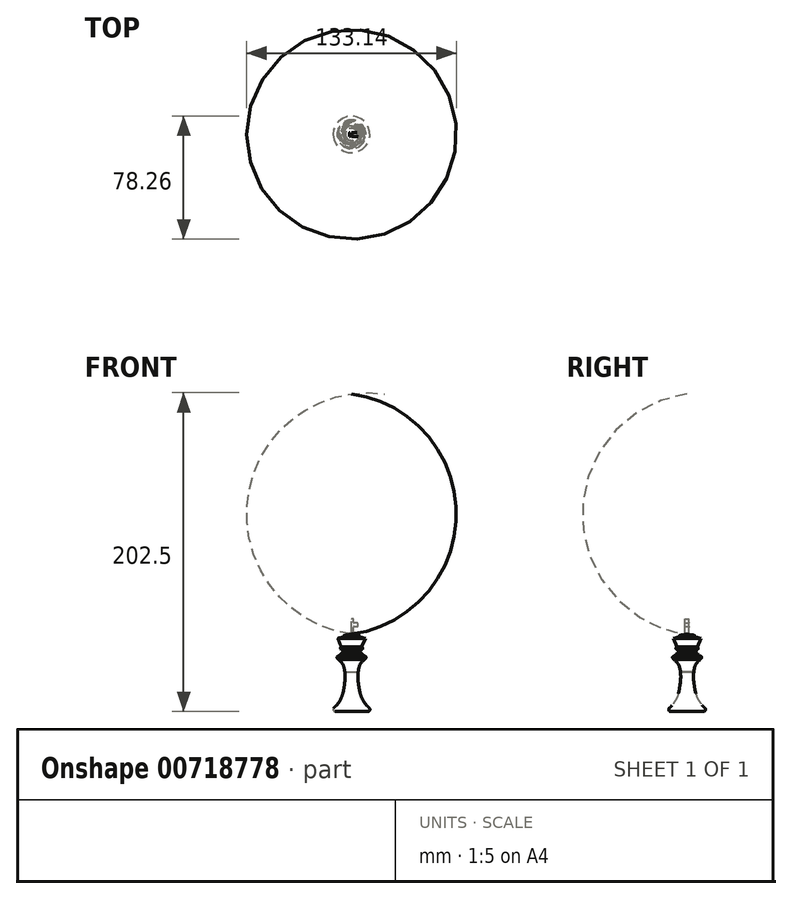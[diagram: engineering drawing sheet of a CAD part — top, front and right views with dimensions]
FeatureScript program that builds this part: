
annotation { "Feature Type Name" : "Feature", "Feature Type Description" : "" }
export const myFeature = defineFeature(function(context is Context, id is Id, definition is map)
    precondition{}
    {
        {
            var Q0;
            Q0=qCreatedBy(makeId("Front.planeOp"),FACE);
            var sketch = newSketch(context, id + "F0", { "sketchPlane" : qUnion([Q0])});
            skLineSegment(sketch, "E0", {"start": v(-6.27, -38.45) * mm, "end": v(13.97, -38.45) * mm});
            skLineSegment(sketch, "E1", {"start": v(9.14, -4.26) * mm, "end": v(9.14, -3.81) * mm});
            skLineSegment(sketch, "E2", {"start": v(7.58, -3.05) * mm, "end": v(5.64, -3.05) * mm});
            skLineSegment(sketch, "E3", {"start": v(5.15, -0.78) * mm, "end": v(5.9, 1.02) * mm});
            skLineSegment(sketch, "E4.MirrorCS", {"start": v(-10.7, 7.6) * mm, "end": v(-5.3, 8.78) * mm});
            skLineSegment(sketch, "E5.MirrorCS", {"start": v(-5.15, -0.78) * mm, "end": v(-8, 8.18) * mm});
            skLineSegment(sketch, "E6.MirrorCS", {"start": v(-7.58, -3.05) * mm, "end": v(-5.64, -3.05) * mm});
            skLineSegment(sketch, "E7.MirrorCS", {"start": v(-9.14, -4.26) * mm, "end": v(-9.14, -3.81) * mm});
            skLineSegment(sketch, "E8.MirrorCS", {"start": v(6.27, -38.45) * mm, "end": v(-13.97, -38.45) * mm});
            skFitSpline(sketch, "E9", {"points": [v(13.97, -38.45) * mm, v(4.51, -21.56) * mm, v(13.97, -2.87) * mm], "startDerivative": vector(-46, 33.89) * mm, "endDerivative": vector(65.38, 22.38) * mm});
            skFitSpline(sketch, "E10.MirrorCS", {"points": [v(-13.97, -38.45) * mm, v(-4.51, -21.56) * mm, v(-13.97, -2.87) * mm], "startDerivative": vector(46, 33.89) * mm, "endDerivative": vector(-65.38, 22.38) * mm});
            skPoint(sketch, "E11.orphan", {"position": v(-9.68, -5.46) * mm});
            skFitSpline(sketch, "E12", {"points": [v(-8.26, -5.46) * mm, v(-4.22, -13.38) * mm], "startDerivative": vector(8.52, -8.35) * mm, "endDerivative": vector(2.36, -15.7) * mm});
            skPoint(sketch, "E13.MirrorP", {"position": v(9.68, -5.46) * mm});
            skFitSpline(sketch, "E14.MirrorCS", {"points": [v(13.97, -38.45) * mm, v(4.51, -21.56) * mm, v(13.97, -2.87) * mm], "startDerivative": vector(-46, 33.89) * mm, "endDerivative": vector(65.38, 22.38) * mm});
            skPoint(sketch, "E15.MirrorCS.1.internal.orphan", {"position": v(4.22, -13.38) * mm});
            skPoint(sketch, "E15.MirrorCS.start.orphan", {"position": v(8.26, -5.46) * mm});
            skFitSpline(sketch, "E16.MirrorCS", {"points": [v(8.26, -5.46) * mm, v(4.22, -13.38) * mm], "startDerivative": vector(-8.52, -8.35) * mm, "endDerivative": vector(-2.36, -15.7) * mm});
            skPoint(sketch, "E17.1.internal.snap0", {"position": v(6.88, 3.45) * mm});
            skFitSpline(sketch, "E17", {"points": [v(5.15, -0.78) * mm, v(6.88, -1.91) * mm, v(5.64, -3.05) * mm], "startDerivative": vector(0.14, -3.1) * mm, "endDerivative": vector(-12.3, 0) * mm});
            skPoint(sketch, "E18.orphan", {"position": v(4.22, -3.05) * mm});
            skFitSpline(sketch, "E19.MirrorCS", {"points": [v(-5.15, -0.78) * mm, v(-6.88, -1.91) * mm, v(-5.64, -3.05) * mm], "startDerivative": vector(-0.14, -3.1) * mm, "endDerivative": vector(12.3, 0) * mm});
            skPoint(sketch, "E20.orphan", {"position": v(-4.42, -3.08) * mm});
            skPoint(sketch, "E21.orphan", {"position": v(-4.22, -3.05) * mm});
            skFitSpline(sketch, "E22", {"points": [v(7.58, -3.05) * mm, v(9.14, -4.26) * mm, v(8.26, -5.46) * mm], "startDerivative": vector(8.74, -1.07) * mm, "endDerivative": vector(-3.54, -2.6) * mm});
            skPoint(sketch, "E23.MirrorCS.start.orphan", {"position": v(9.14, -5.46) * mm});
            skPoint(sketch, "E24.orphan", {"position": v(9.14, -3.05) * mm});
            skFitSpline(sketch, "E25.MirrorCS", {"points": [v(-7.58, -3.05) * mm, v(-9.14, -4.26) * mm, v(-8.26, -5.46) * mm], "startDerivative": vector(-8.74, -1.07) * mm, "endDerivative": vector(3.54, -2.6) * mm});
            skPoint(sketch, "E26.orphan", {"position": v(-9.14, -3.05) * mm});
            skPoint(sketch, "E27.MirrorCS.start.orphan", {"position": v(-9.14, -5.46) * mm});
            skFitSpline(sketch, "E28", {"points": [v(6.5, 2.52) * mm, v(6.88, 2.15) * mm, v(6.88, 1.17) * mm, v(5.9, 1.02) * mm], "startDerivative": vector(1.61, -0.93) * mm, "endDerivative": vector(-3.32, 0.33) * mm});
            skLineSegment(sketch, "E29.trimOffspring", {"start": v(6.5, 2.52) * mm, "end": v(8.75, 8.02) * mm});
            skPoint(sketch, "E30.0.internal.orphan", {"position": v(-5.41, 8.75) * mm});
            skFitSpline(sketch, "E31", {"points": [v(-5.3, 8.78) * mm, v(0, 10.68) * mm], "startDerivative": vector(-2.13, 4.03) * mm, "endDerivative": vector(6.36, 0.91) * mm});
            skFitSpline(sketch, "E32", {"points": [v(-2.12, 10.38) * mm, v(3.25, 10.74) * mm], "startDerivative": vector(-4.73, 9.81) * mm, "endDerivative": vector(-10.34, 10.34) * mm});
            skFitSpline(sketch, "E33", {"points": [v(-2.42, 10.36) * mm, v(0, 11.22) * mm], "startDerivative": vector(0, 0.62) * mm, "endDerivative": vector(5.24, -0.69) * mm});
            skFitSpline(sketch, "E34.MirrorCS", {"points": [v(2.44, 10.6) * mm, v(0, 11.22) * mm], "startDerivative": vector(0, 0.62) * mm, "endDerivative": vector(-5.24, -0.69) * mm});
            skLineSegment(sketch, "E35", {"start": v(-1.2, 11.2) * mm, "end": v(-1.2, 15.49) * mm});
            skLineSegment(sketch, "E36", {"start": v(-1.2, 15.49) * mm, "end": v(-4, 15.49) * mm});
            skLineSegment(sketch, "E37", {"start": v(-4, 15.49) * mm, "end": v(-4, 17.7) * mm});
            skLineSegment(sketch, "E38", {"start": v(-4, 17.7) * mm, "end": v(-1.23, 17.7) * mm});
            skLineSegment(sketch, "E39", {"start": v(-1.23, 17.7) * mm, "end": v(-1.23, 20.45) * mm});
            skLineSegment(sketch, "E40", {"start": v(-1.23, 20.45) * mm, "end": v(0, 20.45) * mm});
            skLineSegment(sketch, "E41.MirrorCS", {"start": v(1.23, 17.7) * mm, "end": v(1.23, 20.45) * mm});
            skLineSegment(sketch, "E42.MirrorCS", {"start": v(4, 17.7) * mm, "end": v(1.23, 17.7) * mm});
            skLineSegment(sketch, "E43.MirrorCS", {"start": v(4, 15.49) * mm, "end": v(4, 17.7) * mm});
            skLineSegment(sketch, "E44.MirrorCS", {"start": v(1.2, 11.2) * mm, "end": v(1.2, 15.49) * mm});
            skLineSegment(sketch, "E45.MirrorCS", {"start": v(1.2, 15.49) * mm, "end": v(4, 15.49) * mm});
            skLineSegment(sketch, "E46.MirrorCS", {"start": v(1.23, 20.45) * mm, "end": v(0, 20.45) * mm});
            skLineSegment(sketch, "E47", {"start": v(0, 11.22) * mm, "end": v(0, 20.45) * mm, "construction": true});
            skLineSegment(sketch, "E48", {"start": v(0, 20.45) * mm, "end": v(0, 11.22) * mm, "construction": true});
            skLineSegment(sketch, "E49", {"start": v(0, 11.22) * mm, "end": v(0, 20.45) * mm});
            skPoint(sketch, "E50.end.orphan", {"position": v(0, 9.38) * mm});
            skLineSegment(sketch, "E51", {"start": v(0, 11.22) * mm, "end": v(0, -38.45) * mm, "construction": true});
            skLineSegment(sketch, "E52", {"start": v(0, -38.45) * mm, "end": v(0, 11.22) * mm});
            skLineSegment(sketch, "E53.MirrorCS", {"start": v(10.7, 7.6) * mm, "end": v(5.3, 8.78) * mm});
            skFitSpline(sketch, "E54.MirrorCS", {"points": [v(5.3, 8.78) * mm, v(0, 10.68) * mm], "startDerivative": vector(2.13, 4.03) * mm, "endDerivative": vector(-6.36, 0.91) * mm});
            skPoint(sketch, "E55.start.orphan", {"position": v(9.54, 9.95) * mm});
            skFitSpline(sketch, "E56.MirrorCS", {"points": [v(2.42, 10.36) * mm, v(0, 11.22) * mm], "startDerivative": vector(0, 0.62) * mm, "endDerivative": vector(-5.24, -0.69) * mm});
            skFitSpline(sketch, "E57", {"points": [v(-11.04, -36.03) * mm, v(-11.76, -35.05) * mm, v(-9.6, -34.55) * mm], "startDerivative": vector(-5.94, 1.01) * mm, "endDerivative": vector(4.48, -1.24) * mm});
            skFitSpline(sketch, "E58.MirrorCS", {"points": [v(11.04, -36.03) * mm, v(11.76, -35.05) * mm, v(9.6, -34.55) * mm], "startDerivative": vector(5.94, 1.01) * mm, "endDerivative": vector(-4.48, -1.24) * mm});
            skFitSpline(sketch, "E59.trimOffspring", {"points": [v(-13.97, -38.45) * mm, v(-4.51, -21.56) * mm, v(-13.97, -2.87) * mm], "startDerivative": vector(46, 33.89) * mm, "endDerivative": vector(-65.38, 22.38) * mm});
            skFitSpline(sketch, "E60.trimOffspring", {"points": [v(13.97, -38.45) * mm, v(4.51, -21.56) * mm, v(13.97, -2.87) * mm], "startDerivative": vector(-46, 33.89) * mm, "endDerivative": vector(65.38, 22.38) * mm});
            skFitSpline(sketch, "E61.trimOffspring", {"points": [v(13.97, -38.45) * mm, v(4.51, -21.56) * mm, v(13.97, -2.87) * mm], "startDerivative": vector(-46, 33.89) * mm, "endDerivative": vector(65.38, 22.38) * mm});
            skFitSpline(sketch, "E62", {"points": [v(-5.17, -25.5) * mm, v(-7.13, -26.44) * mm, v(-5.5, -26.89) * mm], "startDerivative": vector(-4.54, -0.63) * mm, "endDerivative": vector(3.61, 2.7) * mm});
            skFitSpline(sketch, "E63.MirrorCS", {"points": [v(5.17, -25.5) * mm, v(7.13, -26.44) * mm, v(5.5, -26.89) * mm], "startDerivative": vector(4.54, -0.63) * mm, "endDerivative": vector(-3.61, 2.7) * mm});
            skFitSpline(sketch, "E64.trimOffspring", {"points": [v(-13.97, -38.45) * mm, v(-4.51, -21.56) * mm, v(-13.97, -2.87) * mm], "startDerivative": vector(46, 33.89) * mm, "endDerivative": vector(-65.38, 22.38) * mm});
            skFitSpline(sketch, "E65.trimOffspring", {"points": [v(13.97, -38.45) * mm, v(4.51, -21.56) * mm, v(13.97, -2.87) * mm], "startDerivative": vector(-46, 33.89) * mm, "endDerivative": vector(65.38, 22.38) * mm});
            skFitSpline(sketch, "E66.trimOffspring", {"points": [v(13.97, -38.45) * mm, v(4.51, -21.56) * mm, v(13.97, -2.87) * mm], "startDerivative": vector(-46, 33.89) * mm, "endDerivative": vector(65.38, 22.38) * mm});
            skSolve(sketch);
        }
        {
            var Q0;
            {var subQ0=sQuery(id+"F0.wireOp",EDGE,"E0");Q0=makeQuery(id+"F0.imprint","IMPRINT",FACE,{"disambiguationData":[TD([[makeQuery(id+"F0.imprint","IMPRINT",EDGE,{"derivedFrom":subQ0}),1.0]])]});}
            var Q1;
            Q1=sQuery(id+"F0.wireOp",EDGE,"E52");
            revolve(context, id + "F1", {"surfaceOperationType" : NewSurfaceOperationType.NEW, "entities" : qUnion([Q0]), "axis" : qUnion([Q1]), "revolveType" : RevolveType.FULL});
        }
        {
            var Q0;
            Q0=makeQuery(id+"F1.opRevolve","SWEPT_EDGE",EDGE,{"disambiguationData":[OSD([sQuery(id+"F0.wireOp",EDGE,"E0"),sQuery(id+"F0.wireOp",EDGE,"E9")])]});
            fillet(context, id + "F2", {"entities" : qUnion([Q0]), "radius" : 1.27 * mm, "tangentPropagation" : true, "allowEdgeOverflow" : false});
        }
        {
            var Q0;
            {var subQ3=sQuery(id+"F0.wireOp",EDGE,"E35");Q0=makeQuery(id+"F0.imprint","IMPRINT",FACE,{"disambiguationData":[TD([[makeQuery(id+"F0.imprint","IMPRINT",EDGE,{"derivedFrom":subQ3}),-1.0]])]});}
            var Q1;
            Q1=makeQuery(id+"F0.imprint","IMPRINT",FACE,{"disambiguationData":[TD([[makeQuery(id+"F0.imprint","IMPRINT",EDGE,{"derivedFrom":sQuery(id+"F0.wireOp",EDGE,"E41.MirrorCS")}),1.0]])]});
            extrude(context, id + "F3", {"entities" : qUnion([Q0, Q1]), "endBound" : BoundingType.SYMMETRIC, "depth" : 2.54 * mm, "offsetDistance" : 25.4 * mm});
        }
        {
            var Q0;
            Q0=makeQuery(id+"F3.opExtrude","SWEPT_EDGE",EDGE,{"disambiguationData":[OSD([sQuery(id+"F0.wireOp",EDGE,"E39"),sQuery(id+"F0.wireOp",EDGE,"E40")])]});
            var Q1;
            Q1=makeQuery(id+"F3.opExtrude","SWEPT_EDGE",EDGE,{"disambiguationData":[OSD([sQuery(id+"F0.wireOp",EDGE,"E41.MirrorCS"),sQuery(id+"F0.wireOp",EDGE,"E46.MirrorCS")])]});
            var Q2;
            Q2=makeQuery(id+"F3.opExtrude","SWEPT_EDGE",EDGE,{"disambiguationData":[OSD([sQuery(id+"F0.wireOp",EDGE,"E42.MirrorCS"),sQuery(id+"F0.wireOp",EDGE,"E43.MirrorCS")])]});
            var Q3;
            Q3=makeQuery(id+"F3.opExtrude","SWEPT_EDGE",EDGE,{"disambiguationData":[OSD([sQuery(id+"F0.wireOp",EDGE,"E37"),sQuery(id+"F0.wireOp",EDGE,"E38")])]});
            var Q4;
            Q4=makeQuery(id+"F3.opExtrude","SWEPT_EDGE",EDGE,{"disambiguationData":[OSD([sQuery(id+"F0.wireOp",EDGE,"E43.MirrorCS"),sQuery(id+"F0.wireOp",EDGE,"E45.MirrorCS")])]});
            var Q5;
            Q5=makeQuery(id+"F3.opExtrude","SWEPT_EDGE",EDGE,{"disambiguationData":[OSD([sQuery(id+"F0.wireOp",EDGE,"E36"),sQuery(id+"F0.wireOp",EDGE,"E37")])]});
            var Q6;
            Q6=makeQuery(id+"F3.opExtrude","SWEPT_EDGE",EDGE,{"disambiguationData":[OSD([sQuery(id+"F0.wireOp",EDGE,"E35"),sQuery(id+"F0.wireOp",EDGE,"E36")])]});
            var Q7;
            Q7=makeQuery(id+"F3.opExtrude","SWEPT_EDGE",EDGE,{"disambiguationData":[OSD([sQuery(id+"F0.wireOp",EDGE,"E44.MirrorCS"),sQuery(id+"F0.wireOp",EDGE,"E45.MirrorCS")])]});
            var Q8;
            Q8=makeQuery(id+"F3.opExtrude","SWEPT_EDGE",EDGE,{"disambiguationData":[OSD([sQuery(id+"F0.wireOp",EDGE,"E41.MirrorCS"),sQuery(id+"F0.wireOp",EDGE,"E42.MirrorCS")])]});
            var Q9;
            Q9=makeQuery(id+"F3.opExtrude","SWEPT_EDGE",EDGE,{"disambiguationData":[OSD([sQuery(id+"F0.wireOp",EDGE,"E38"),sQuery(id+"F0.wireOp",EDGE,"E39")])]});
            fillet(context, id + "F4", {"entities" : qUnion([Q0, Q1, Q2, Q3, Q4, Q5, Q6, Q7, Q8, Q9]), "radius" : 0.38 * mm, "tangentPropagation" : true, "allowEdgeOverflow" : false});
        }
    });
